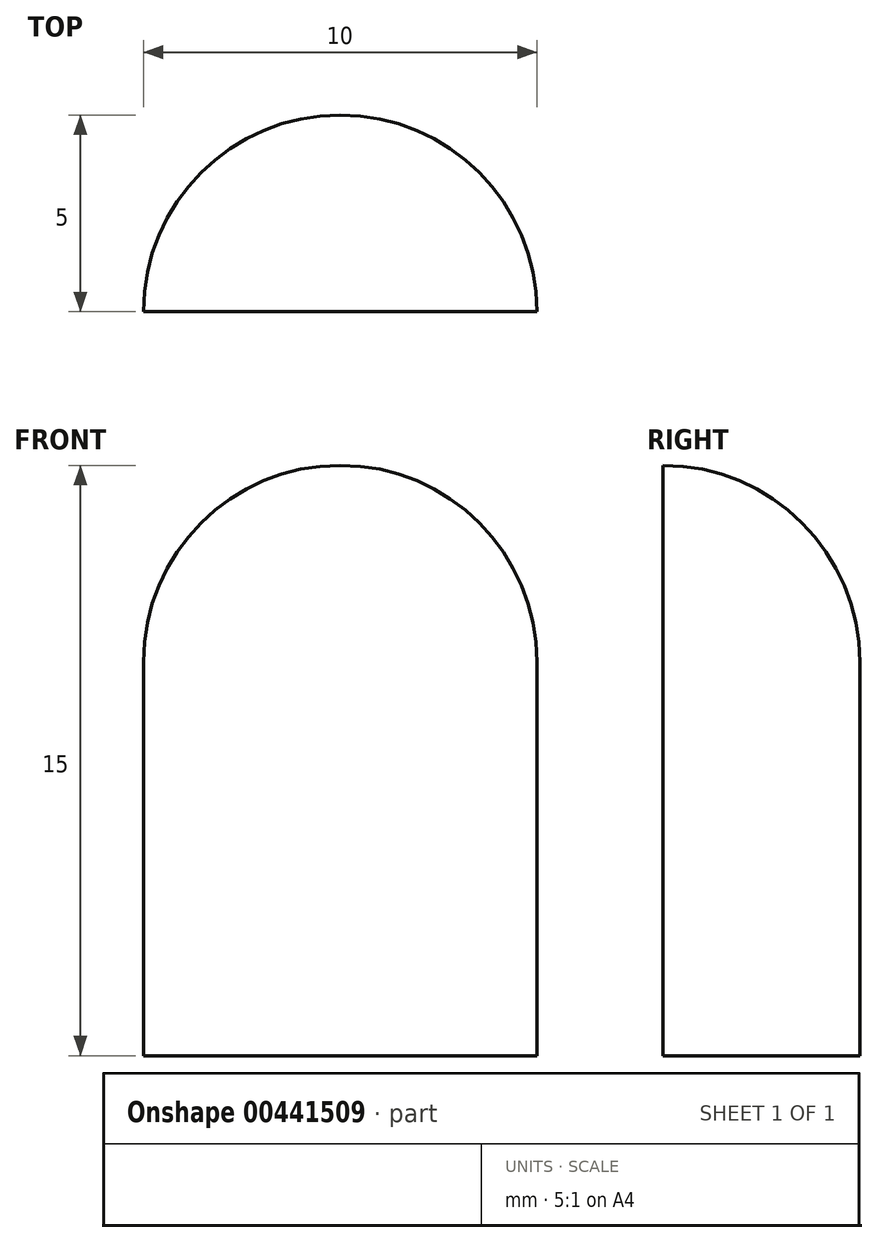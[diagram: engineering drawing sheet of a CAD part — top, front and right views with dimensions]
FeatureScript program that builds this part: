
annotation { "Feature Type Name" : "Feature", "Feature Type Description" : "" }
export const myFeature = defineFeature(function(context is Context, id is Id, definition is map)
    precondition{}
    {
        {
            var Q0;
            Q0=qCreatedBy(makeId("Front.planeOp"),FACE);
            var sketch = newSketch(context, id + "F0", { "sketchPlane" : qUnion([Q0])});
            skArc(sketch, "E0", {"start": v(5, 0) * mm, "mid": v(3.54, 3.54) * mm, "end": v(0, 5) * mm});
            skLineSegment(sketch, "E1", {"start": v(0, -10) * mm, "end": v(5, -10) * mm});
            skLineSegment(sketch, "E2", {"start": v(5, -10) * mm, "end": v(5, 0) * mm});
            skLineSegment(sketch, "E3", {"start": v(0, -10) * mm, "end": v(0, 5) * mm});
            skSolve(sketch);
        }
        {
            var Q0;
            Q0=qSketchRegion(id+"F0",true);
            var Q1;
            Q1=sQuery(id+"F0.wireOp",EDGE,"E3");
            revolve(context, id + "F1", {"entities" : qUnion([Q0]), "axis" : qUnion([Q1]), "revolveType" : RevolveType.ONE_DIRECTION, "angle" : 180 * degree});
        }
    });
